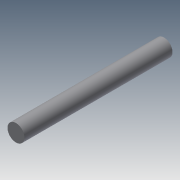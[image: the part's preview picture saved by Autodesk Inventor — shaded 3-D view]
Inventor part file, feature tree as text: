
AUTODESK INVENTOR PART (.ipt)
format: ipt  version: 2013 (Build 170138000, 138)  size: 71,680 bytes
history: native  units: mm
features: extrude x2, sketch x2
ambient origin geometry x8: Origin, YZ Plane, XZ Plane, XY Plane, X Axis, Y Axis, Z Axis, Center Point
bodies: Solid1 (feature_tree)
feature tree (4):
  extrude  "Extrusion1"  Depth=28.0mm TaperAngle=0.0deg
  extrude  "Extrusion2"  [1 undecoded]
  sketch  "Sketch1"  dims[d0=4.0mm d1=28.0mm d2=0.0mm]
  sketch  "Sketch2"  dims[d3=7.0mm d4=0.0mm]
note: 1 required parameter value undecoded (feature->parameter linkage not recoverable at this tier; creation-order binding heuristic only, values carry confidence <= 0.55)
